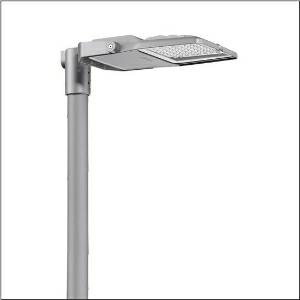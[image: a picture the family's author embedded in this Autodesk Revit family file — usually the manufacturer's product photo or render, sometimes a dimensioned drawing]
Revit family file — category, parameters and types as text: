
# Revit family: floodlight_fl_21_iq_mini___pl64_5xa7771d4e3a_aa37
name_source: partatom
category: Lighting Fixtures
units: mm (PartAtom-declared; Revit-internal decimal feet)

## family parameters
Cut with Voids When Loaded = No
Host = Face
Light Source = No
Part Type = Normal
Room Calculation Point = No
Round Connector Dimension = Use Diameter
Shared = No

## types (1)
- --- (1 x LED, 17970 lm, 143 W, 4000K)
    Apparent Load = 143 VA
    CIE Flux Codes = 28 80 98 100 100
    Color Rendering = 70
    Color Temperature = 4000K
    Default Elevation = 1800 mm
    Description = Floodlight FL 21 iQ mini, floodlight, primary light control with lens, of PMMA, primary optical cover: protective disc, of toughened safety glass, transparent, light distribution: PL64, light emission: direct distribution, installation type: surface-mounted, LED, High Power LED, rated luminous flux: 17.970lm, luminous efficacy: 126lm/W, light colour: 740, colour temperature: 4000K, control gear: iQ Comfort/DALI, control: Auto-Match, Temp-Guard, Lumen-Switch, Night-Set, Smart-Wire, Light-Fading, Desk-Remote (wireless, voltage-free reading and setting of iQ features in the workshop via application-optimized NFC function/RFID function), optimised constant luminous flux control (CLO 2.0), with terminal, 6-pole, mains connection: 220..240V, AC, 50/60Hz, start of lifetime: 143W, end of service life: 152W, reduction: 61W, luminaire housing, of diecast aluminium, powder-coated, Siteco® metallic grey (DB 702S), corrosivity category C5 mid according to DIN EN ISO 12944, suitable for swimming pools, chlorine-resistant, sealing non-destructively replaceable, please order mast flange separately, mast bracket, of steel, galvanised, powder-coated, Siteco® metallic grey (DB 702S), protection rating (complete): IP66, insulation class (complete): insulation class II (safety insulation), certification: CE, ENEC, VDE, protection symbol: D, impact resistance: IK08, permissible operating ambient temperature: -40..+40°C, permissible operating ambient temperature for outdoor applications: -40..+50°C, standard: DIN EN 12944, LABS conformity tested according to VDMA 24364:2018-05, packaging unit: 1 piece

Light Distribution: PL64
    Height = 70 mm
    Lamp = 1 x LED
    Lamp Light Flux = 17970 lm
    Lamp Power = 143 W
    Lamp count = 1
    Length = 485 mm
    Luminous efficacy = 126 lm/W
    Manufacturer = Siteco
    ModVariant = No
    Model = 5XA7771D4E3A
    Number of Poles = 1
    OnlyDefault = Yes
    Power Factor = 1
    Product Name = Floodlight FL 21 iQ mini | PL64
    Product group = floodlight | pylon annexe
    ProductGroupID = 6200
    Protection Class = Protection class II
    Protection Degree = IP 66
    RLX_Detail_Level = 1
    RLX_Emergency_Light_Flux = 0 lm
    RLX_Emergency_Type = 0
    RLX_Emergency_Type_DB = No
    RlxData = <blob elided: 101725 chars, md5=1f4b4502>
    Socket = socket
    Standby Power = 0 W
    System Light Flux = 17970 lm
    System Power = 143 W
    Type Comments = factory setting: luminous flux: 100 % | dim-lin: 254 | 730 mA
    Type Image = l_1007125.jpg
    URL = http://relux.com
    VarID = @adj_165954
    Voltage = 0 V
    Weight = 0.00 kg
    Width = 337 mm

## geometry (parser evidence)
native form markers: Blend x4, Sweep x11
no freeform markers — native parametric forms only
